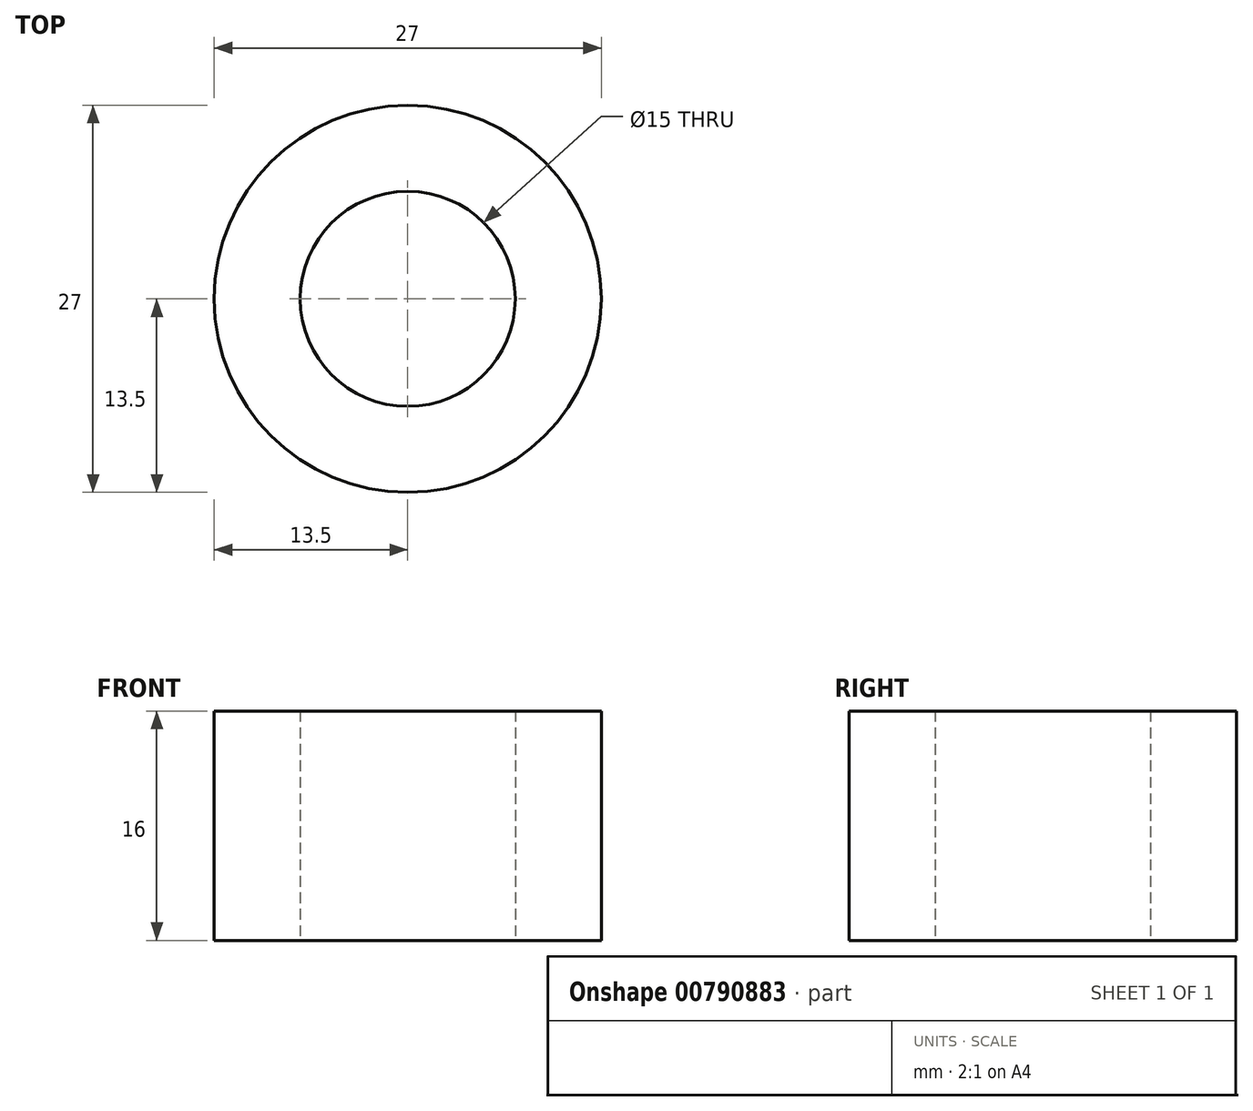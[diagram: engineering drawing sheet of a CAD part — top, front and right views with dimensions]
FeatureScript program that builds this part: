
annotation { "Feature Type Name" : "Feature", "Feature Type Description" : "" }
export const myFeature = defineFeature(function(context is Context, id is Id, definition is map)
    precondition{}
    {
        {
            var Q0;
            Q0=qCreatedBy(makeId("Top.planeOp"),FACE);
            var sketch = newSketch(context, id + "F0", { "sketchPlane" : qUnion([Q0])});
            skCircle(sketch, "E0", {"center": v(0, 0) * mm, "radius": 7.5 * mm});
            skCircle(sketch, "E1", {"center": v(0, 0) * mm, "radius": 13.5 * mm});
            skSolve(sketch);
        }
        {
            var Q0;
            Q0 = qSketchRegion(id + "F0", true);
            extrude(context, id + "F1", {"entities" : qUnion([Q0]), "depth" : 16 * mm, "offsetDistance" : 25 * mm});
        }
    });
